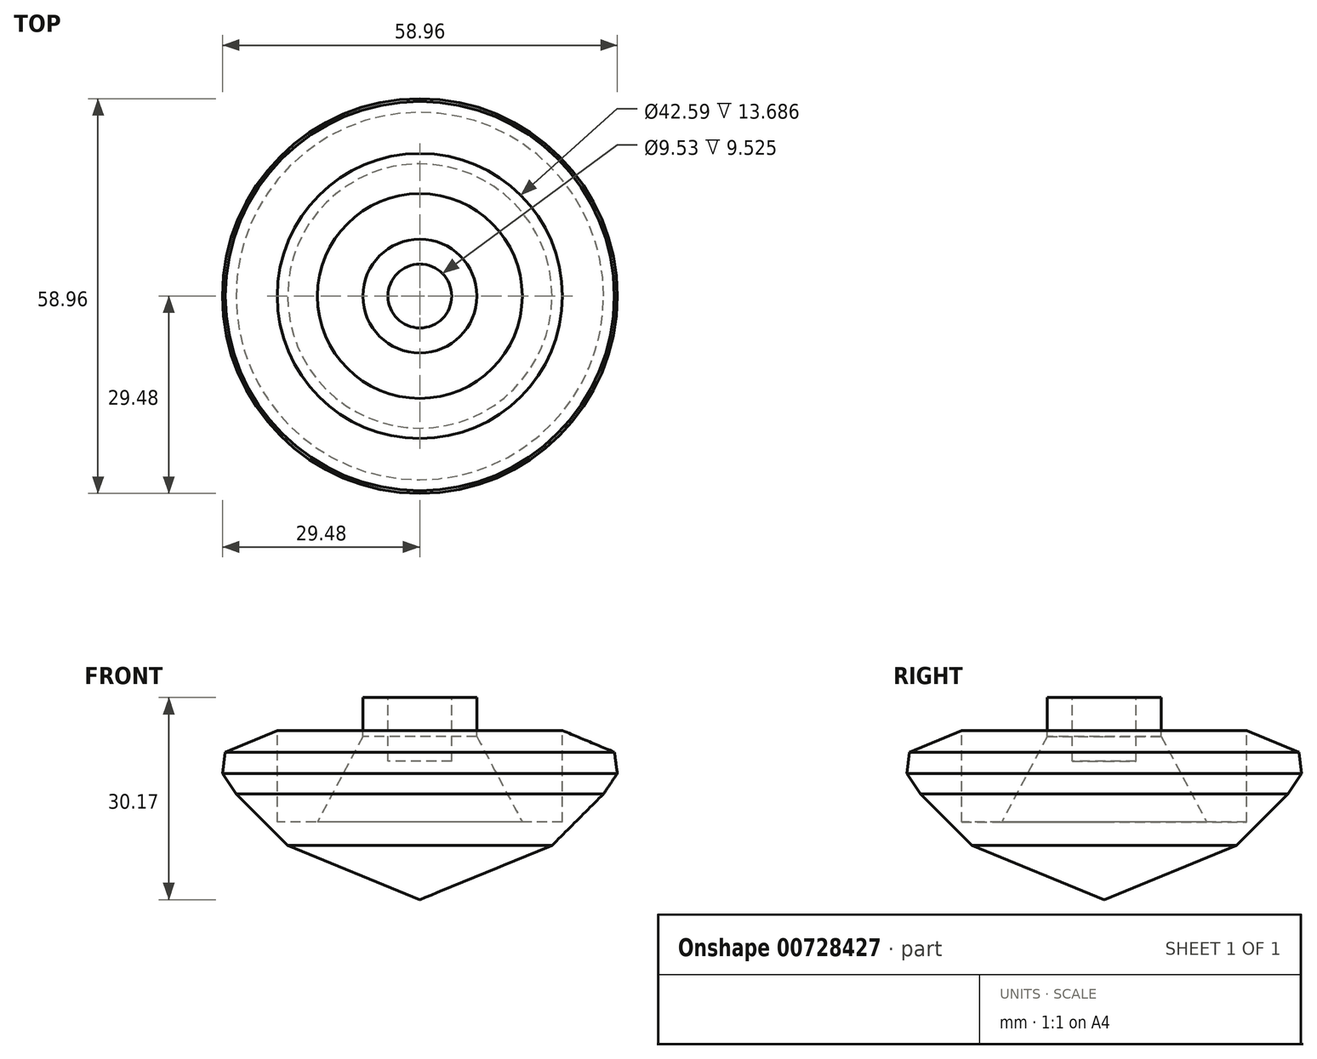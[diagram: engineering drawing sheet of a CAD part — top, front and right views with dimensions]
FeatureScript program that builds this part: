
annotation { "Feature Type Name" : "Feature", "Feature Type Description" : "" }
export const myFeature = defineFeature(function(context is Context, id is Id, definition is map)
    precondition{}
    {
        {
            var Q0;
            Q0=qCreatedBy(makeId("Front.planeOp"),FACE);
            var sketch = newSketch(context, id + "F0", { "sketchPlane" : qUnion([Q0])});
            skLineSegment(sketch, "E0", {"start": v(0, 0) * mm, "end": v(19.74, 8.1) * mm});
            skLineSegment(sketch, "E1", {"start": v(19.74, 8.1) * mm, "end": v(27.44, 15.8) * mm});
            skLineSegment(sketch, "E2", {"start": v(27.44, 15.8) * mm, "end": v(29.48, 18.86) * mm});
            skLineSegment(sketch, "E3", {"start": v(21.3, 25.26) * mm, "end": v(21.3, 11.58) * mm});
            skLineSegment(sketch, "E4", {"start": v(21.3, 11.58) * mm, "end": v(15.3, 11.58) * mm});
            skLineSegment(sketch, "E5", {"start": v(15.3, 11.58) * mm, "end": v(8.5, 24.38) * mm});
            skLineSegment(sketch, "E6", {"start": v(8.5, 24.38) * mm, "end": v(8.5, 30.17) * mm});
            skLineSegment(sketch, "E7", {"start": v(0, 30.17) * mm, "end": v(0, 0) * mm});
            skLineSegment(sketch, "E8", {"start": v(8.5, 30.17) * mm, "end": v(0, 30.17) * mm});
            skLineSegment(sketch, "E9", {"start": v(29.48, 18.86) * mm, "end": v(29.06, 22.02) * mm});
            skPoint(sketch, "E10.start.orphan", {"position": v(20.28, 24.38) * mm});
            skLineSegment(sketch, "E11", {"start": v(29.06, 22.02) * mm, "end": v(21.3, 25.26) * mm});
            skSolve(sketch);
        }
        {
            var Q0;
            Q0=makeQuery(id+"F0.imprint","IMPRINT",FACE,{"disambiguationData":[TD([[makeQuery(id+"F0.imprint","IMPRINT",EDGE,{"derivedFrom":sQuery(id+"F0.wireOp",EDGE,"E0")}),1.0]])]});
            var Q1;
            Q1=sQuery(id+"F0.wireOp",EDGE,"E7");
            revolve(context, id + "F1", {"surfaceOperationType" : NewSurfaceOperationType.NEW, "entities" : qUnion([Q0]), "axis" : qUnion([Q1]), "revolveType" : RevolveType.FULL});
        }
        {
            var Q0;
            Q0=makeQuery(id+"F1.opRevolve","SWEPT_FACE",FACE,{"disambiguationData":[OSD([sQuery(id+"F0.wireOp",EDGE,"E8")])]});
            var sketch = newSketch(context, id + "F2", { "sketchPlane" : qUnion([Q0])});
            skCircle(sketch, "E12", {"center": v(0, 0) * mm, "radius": 4.76 * mm});
            skSolve(sketch);
        }
        {
            var Q0;
            Q0=makeQuery(id+"F2.imprint","IMPRINT",FACE,{"disambiguationData":[TD([[makeQuery(id+"F2.imprint","IMPRINT",EDGE,{"derivedFrom":sQuery(id+"F2.wireOp",EDGE,"E12")}),1.0]])]});
            extrude(context, id + "F3", {"entities" : qUnion([Q0]), "operationType" : NewBodyOperationType.REMOVE, "oppositeDirection" : true, "depth" : 9.52 * mm, "offsetDistance" : 25.4 * mm});
        }
    });
